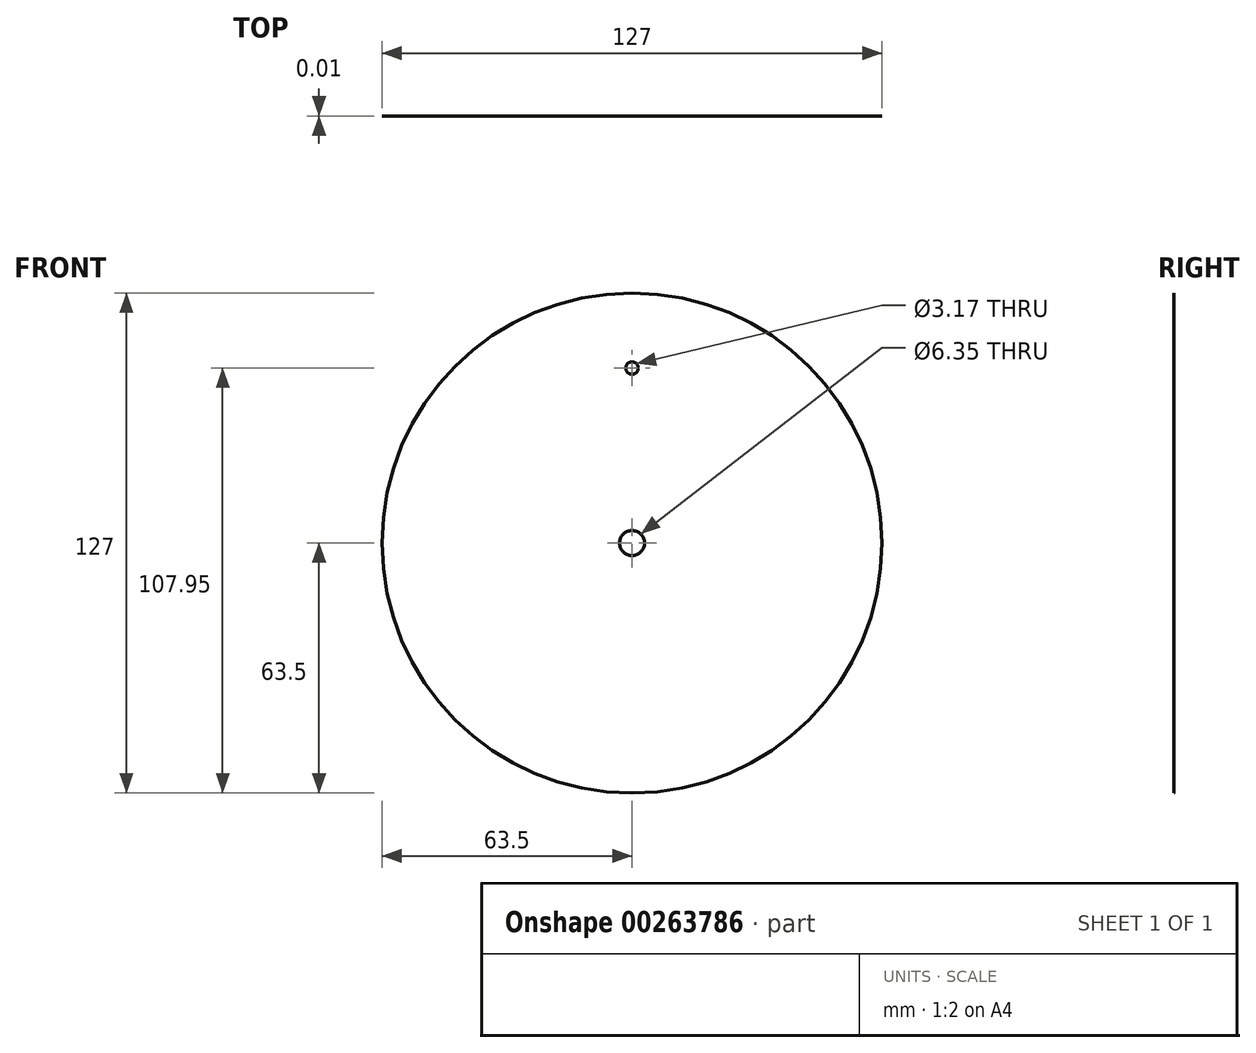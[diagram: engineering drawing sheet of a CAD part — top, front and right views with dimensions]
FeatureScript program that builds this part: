
annotation { "Feature Type Name" : "Feature", "Feature Type Description" : "" }
export const myFeature = defineFeature(function(context is Context, id is Id, definition is map)
    precondition{}
    {
        {
            var Q0;
            Q0=qCreatedBy(makeId("Front.planeOp"),FACE);
            var sketch = newSketch(context, id + "F0", { "sketchPlane" : qUnion([Q0])});
            skCircle(sketch, "E0", {"center": v(0, 0) * mm, "radius": 3.18 * mm});
            skCircle(sketch, "E1", {"center": v(0, 0) * mm, "radius": 63.5 * mm});
            skCircle(sketch, "E2", {"center": v(0, 44.45) * mm, "radius": 1.59 * mm});
            skSolve(sketch);
        }
        {
            var Q0;
            Q0=qSketchRegion(id+"F0",true);
            extrude(context, id + "F1", {"entities" : qUnion([Q0]), "depth" : 1 / 101.6 * mm});
        }
    });
